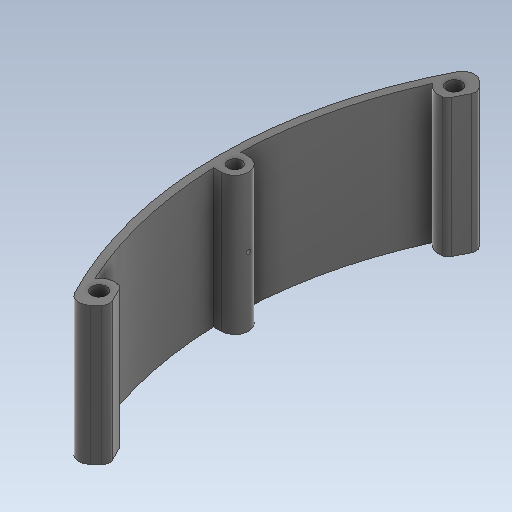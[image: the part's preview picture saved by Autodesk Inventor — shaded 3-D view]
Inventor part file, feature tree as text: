
AUTODESK INVENTOR PART (.ipt)
format: ipt  version: 2020 (Build 240168000, 168)  size: 1,289,216 bytes
history: native  units: mm
features: extrude x12, sketch x9, projected_geometry x9, other x3, fillet x2
ambient origin geometry x8: Origin, YZ Plane, XZ Plane, XY Plane, X Axis, Y Axis, Z Axis, Center Point
bodies: Body1 (feature_tree)
feature tree (35):
  other  "Твердое тело1"
  extrude  "outer"  TaperAngle=45.0deg  [1 undecoded]
  extrude  "inner"  Depth=7.0mm
  sketch  "Эскиз3"
  extrude  "Выдавливание3"  Depth=20.0mm
  extrude  "Выдавливание4"  Depth=7.0mm
  sketch  "Эскиз4"
  extrude  "Выдавливание5"  Depth=3.2mm
  extrude  "Выдавливание6"  Depth=59.0mm
  sketch  "Эскиз5"
  extrude  "Выдавливание7"  Depth=83.0mm
  extrude  "Выдавливание8"  Depth=69.0mm
  sketch  "Эскиз6"
  extrude  "Выдавливание9"  Depth=55.0mm
  extrude  "Выдавливание10"  Depth=3.0mm
  fillet  "Сопряжение1"  Radius=8.0mm
  other  "РабПлоскость2"
  sketch  "Эскиз8"
  extrude  "Выдавливание11"  Depth=5.0mm
  fillet  "Сопряжение2"  Radius=2.0mm
  sketch  "3D эскиз1"
  extrude  "Выдавливание12"  Depth=40.0mm TaperAngle=360.0deg
  sketch  "Эскиз1"
  sketch  "Эскиз2"
  projected_geometry  "Спроецированная петля1"
  projected_geometry  "Спроецированная петля2"
  projected_geometry  "Спроецированная петля3"
  projected_geometry  "Спроецированная петля4"
  projected_geometry  "Спроецированная петля5"
  projected_geometry  "Спроецированная петля8"
  projected_geometry  "Спроецированная петля9"
  projected_geometry  "Спроецированная петля10"
  other  "Проецирование на поверхность1"
  sketch  "Эскиз10"
  projected_geometry  "Спроецированная петля11"
note: 1 required parameter value undecoded (feature->parameter linkage not recoverable at this tier; creation-order binding heuristic only, values carry confidence <= 0.55)
